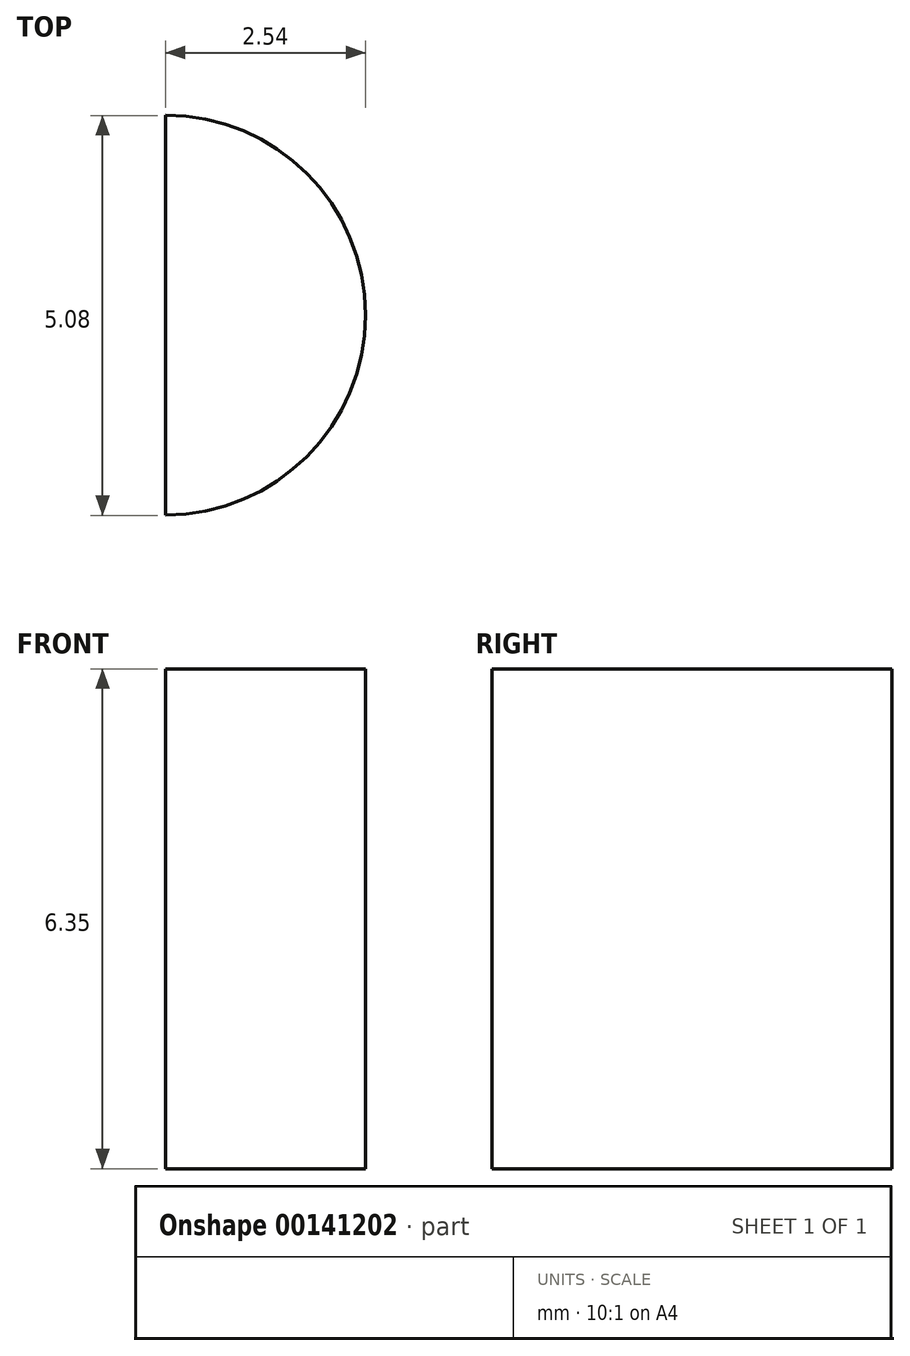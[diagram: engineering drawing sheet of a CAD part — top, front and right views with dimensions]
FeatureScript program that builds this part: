
annotation { "Feature Type Name" : "Feature", "Feature Type Description" : "" }
export const myFeature = defineFeature(function(context is Context, id is Id, definition is map)
    precondition{}
    {
        {
            var Q0;
            Q0=qCreatedBy(makeId("Top.planeOp"),FACE);
            var sketch = newSketch(context, id + "F0", { "sketchPlane" : qUnion([Q0])});
            skLineSegment(sketch, "E0", {"start": v(-37.12, 31.02) * mm, "end": v(-37.12, 25.94) * mm});
            skArc(sketch, "E1", {"start": v(-37.12, 25.94) * mm, "mid": v(-34.58, 28.48) * mm, "end": v(-37.12, 31.02) * mm});
            skSolve(sketch);
        }
        {
            var Q0;
            Q0=makeQuery(id+"F0.imprint","IMPRINT",FACE,{"disambiguationData":[TD([[makeQuery(id+"F0.imprint","IMPRINT",EDGE,{"derivedFrom":sQuery(id+"F0.wireOp",EDGE,"E0")}),1.0]])]});
            extrude(context, id + "F1", {"entities" : qUnion([Q0]), "depth" : 6.35 * mm});
        }
    });
